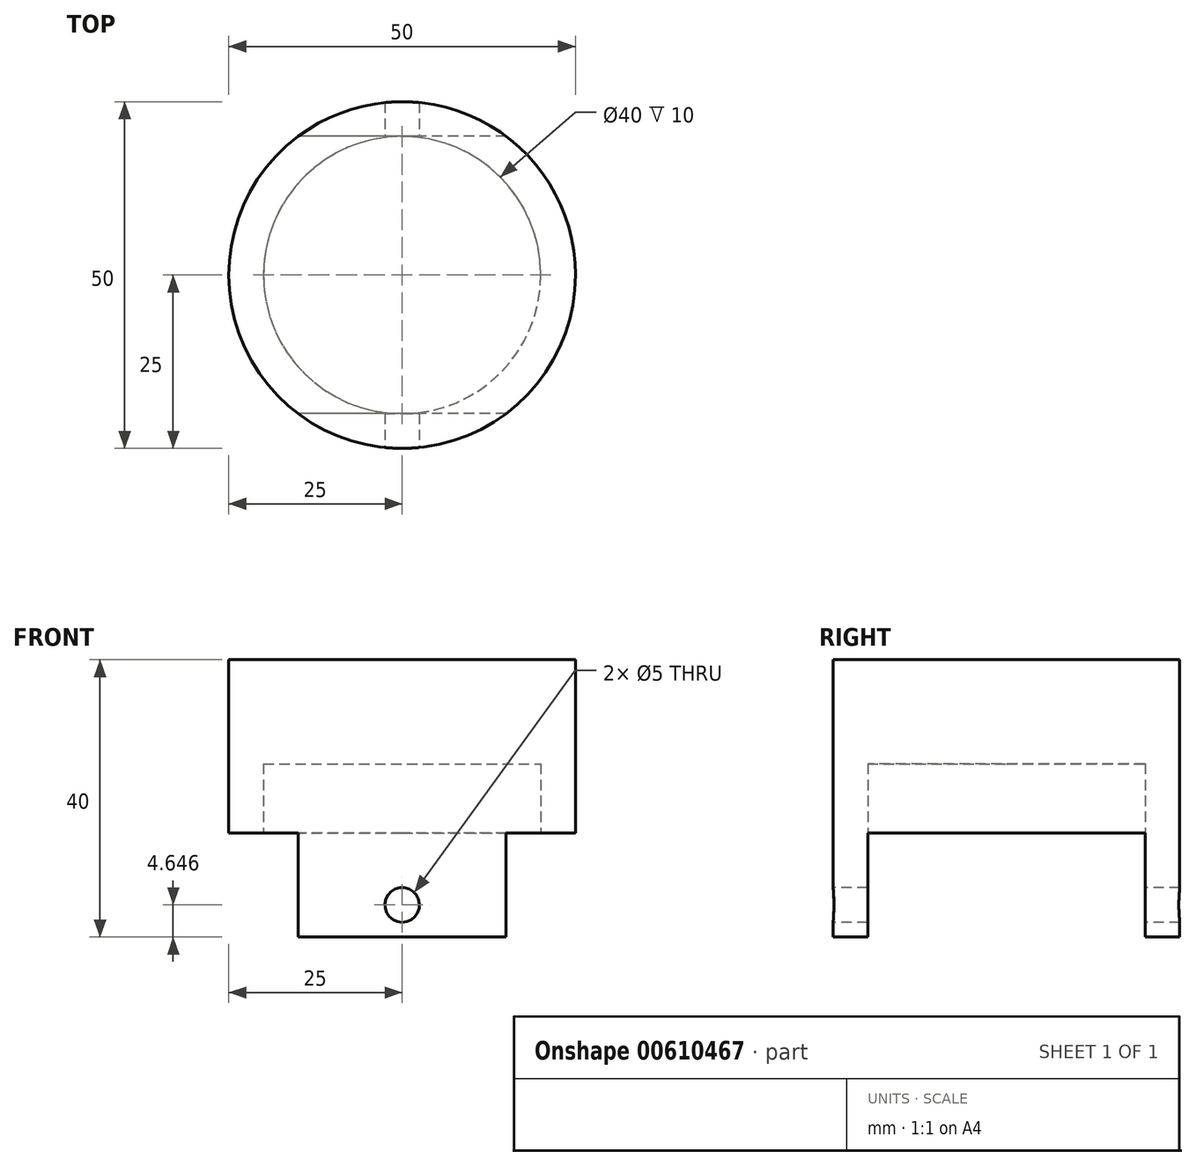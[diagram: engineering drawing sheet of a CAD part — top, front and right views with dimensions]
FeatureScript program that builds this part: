
annotation { "Feature Type Name" : "Feature", "Feature Type Description" : "" }
export const myFeature = defineFeature(function(context is Context, id is Id, definition is map)
    precondition{}
    {
        {
            var Q0;
            Q0=qCreatedBy(makeId("Top.planeOp"),FACE);
            var sketch = newSketch(context, id + "F0", { "sketchPlane" : qUnion([Q0])});
            skCircle(sketch, "E0", {"center": v(0, 0) * mm, "radius": 25 * mm});
            skSolve(sketch);
        }
        {
            var Q0;
            Q0 = qSketchRegion(id + "F0", true);
            extrude(context, id + "F1", {"entities" : qUnion([Q0]), "depth" : 40 * mm, "offsetDistance" : 25 * mm});
        }
        {
            var Q0;
            Q0=makeQuery(id+"F1.opExtrude","CAP_FACE",FACE,{"disambiguationData":[OSD([sQuery(id+"F0.wireOp",EDGE,"E0")])],"isStart":true});
            var sketch = newSketch(context, id + "F2", { "sketchPlane" : qUnion([Q0])});
            skPoint(sketch, "E1.middle", {"position": v(0, 0) * mm});
            skLineSegment(sketch, "E2.bottom", {"start": v(33.56, 20) * mm, "end": v(-33.56, 20) * mm});
            skLineSegment(sketch, "E2.top", {"start": v(33.56, -20) * mm, "end": v(-33.56, -20) * mm});
            skLineSegment(sketch, "E2.left", {"start": v(33.56, 20) * mm, "end": v(33.56, -20) * mm});
            skLineSegment(sketch, "E2.right", {"start": v(-33.56, 20) * mm, "end": v(-33.56, -20) * mm});
            skSolve(sketch);
        }
        {
            var Q0;
            Q0 = qSketchRegion(id + "F2", true);
            extrude(context, id + "F3", {"entities" : qUnion([Q0]), "operationType" : NewBodyOperationType.REMOVE, "oppositeDirection" : true, "depth" : 15 * mm, "offsetDistance" : 25 * mm});
        }
        {
            var Q0;
            Q0=makeQuery(id+"F3.boolean.opBoolean","COPY",FACE,{"derivedFrom":makeQuery(id+"F3.opExtrude","CAP_FACE",FACE,{"disambiguationData":[OSD([sQuery(id+"F2.wireOp",EDGE,"E2.bottom"),sQuery(id+"F2.wireOp",EDGE,"E2.top"),sQuery(id+"F2.wireOp",EDGE,"E2.left"),sQuery(id+"F2.wireOp",EDGE,"E2.right")])],"isStart":false})});
            var sketch = newSketch(context, id + "F4", { "sketchPlane" : qUnion([Q0])});
            skCircle(sketch, "E3", {"center": v(0, 0) * mm, "radius": 20 * mm});
            skSolve(sketch);
        }
        {
            var Q0;
            Q0 = qSketchRegion(id + "F4", true);
            extrude(context, id + "F5", {"entities" : qUnion([Q0]), "operationType" : NewBodyOperationType.REMOVE, "oppositeDirection" : true, "depth" : 10 * mm, "offsetDistance" : 25 * mm});
        }
        {
            var Q0;
            Q0=qCreatedBy(makeId("Front.planeOp"),FACE);
            var sketch = newSketch(context, id + "F6", { "sketchPlane" : qUnion([Q0])});
            skCircle(sketch, "E4", {"center": v(0, 4.65) * mm, "radius": 2.5 * mm});
            skSolve(sketch);
        }
        {
            var Q0;
            Q0 = qSketchRegion(id + "F6", true);
            extrude(context, id + "F7", {"entities" : qUnion([Q0]), "operationType" : NewBodyOperationType.REMOVE, "endBound" : BoundingType.SYMMETRIC, "oppositeDirection" : true, "depth" : 100 * mm, "offsetDistance" : 25 * mm});
        }
    });
